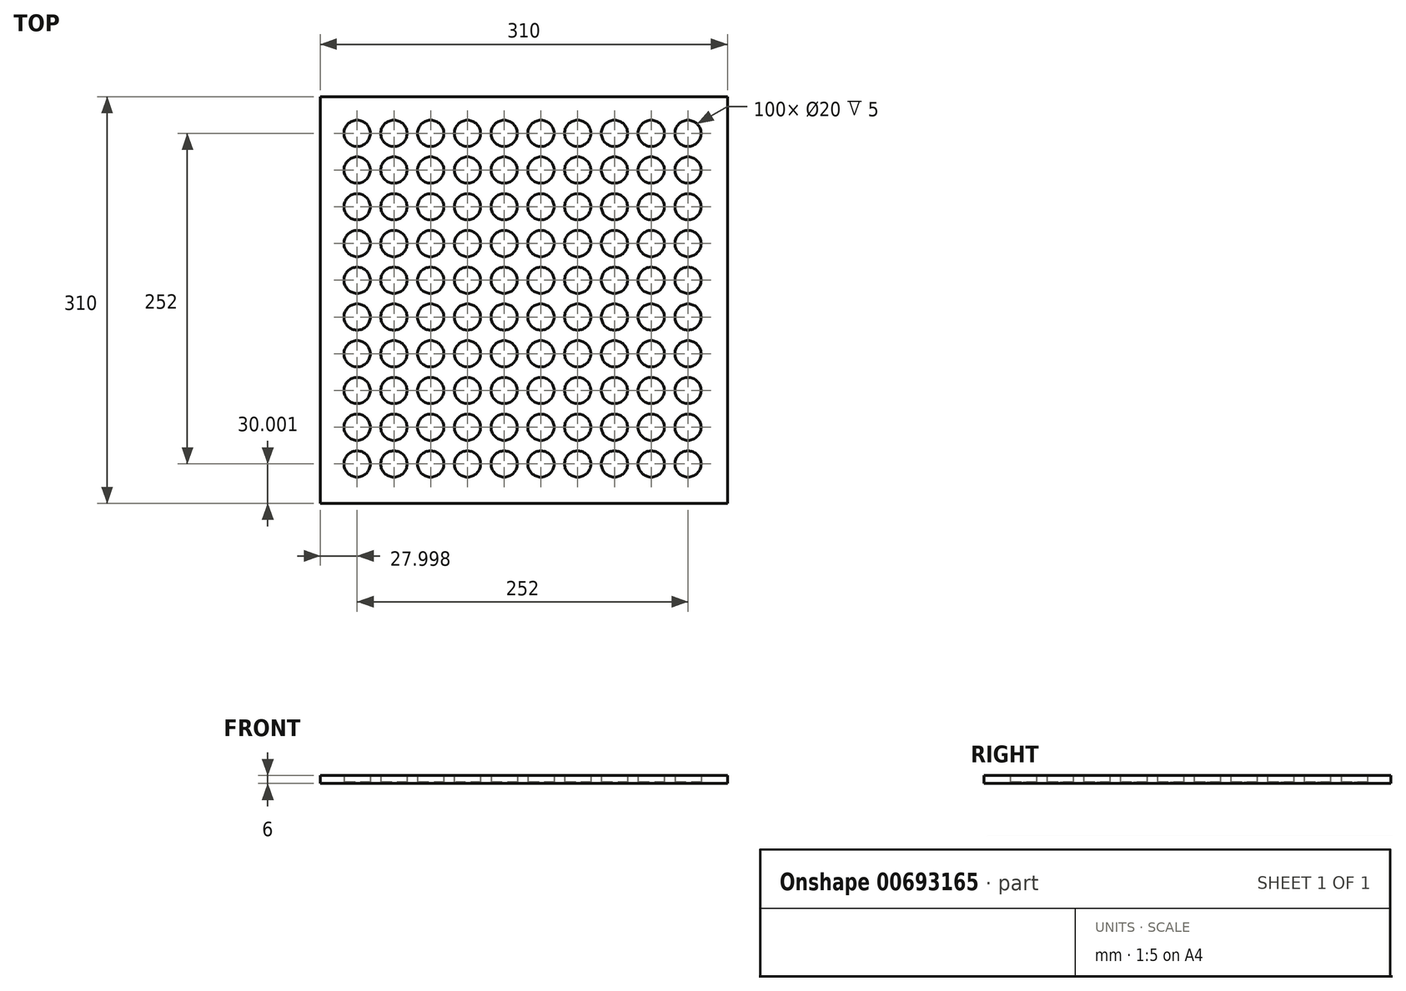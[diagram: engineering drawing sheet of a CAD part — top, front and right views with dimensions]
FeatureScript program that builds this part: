
annotation { "Feature Type Name" : "Feature", "Feature Type Description" : "" }
export const myFeature = defineFeature(function(context is Context, id is Id, definition is map)
    precondition{}
    {
        {
            var Q0;
            Q0=qCreatedBy(makeId("Top.planeOp"),FACE);
            var sketch = newSketch(context, id + "F0", { "sketchPlane" : qUnion([Q0])});
            skLineSegment(sketch, "E0.bottom", {"start": v(-288.8, 191.74) * mm, "end": v(21.2, 191.74) * mm});
            skLineSegment(sketch, "E0.top", {"start": v(-288.8, -118.26) * mm, "end": v(21.2, -118.26) * mm});
            skLineSegment(sketch, "E0.left", {"start": v(-288.8, 191.74) * mm, "end": v(-288.8, -118.26) * mm});
            skLineSegment(sketch, "E0.right", {"start": v(21.2, 191.74) * mm, "end": v(21.2, -118.26) * mm});
            skCircle(sketch, "E1", {"center": v(-260.8, 163.74) * mm, "radius": 10 * mm});
            skCircle(sketch, "E2.0.1.0", {"center": v(-260.8, 135.74) * mm, "radius": 10 * mm});
            skCircle(sketch, "E2.0.2.0", {"center": v(-260.8, 107.74) * mm, "radius": 10 * mm});
            skCircle(sketch, "E2.0.3.0", {"center": v(-260.8, 79.74) * mm, "radius": 10 * mm});
            skCircle(sketch, "E2.0.4.0", {"center": v(-260.8, 51.74) * mm, "radius": 10 * mm});
            skCircle(sketch, "E2.1.0.0", {"center": v(-232.8, 163.74) * mm, "radius": 10 * mm});
            skCircle(sketch, "E2.1.1.0", {"center": v(-232.8, 135.74) * mm, "radius": 10 * mm});
            skCircle(sketch, "E2.1.2.0", {"center": v(-232.8, 107.74) * mm, "radius": 10 * mm});
            skCircle(sketch, "E2.1.3.0", {"center": v(-232.8, 79.74) * mm, "radius": 10 * mm});
            skCircle(sketch, "E2.1.4.0", {"center": v(-232.8, 51.74) * mm, "radius": 10 * mm});
            skCircle(sketch, "E2.2.0.0", {"center": v(-204.8, 163.74) * mm, "radius": 10 * mm});
            skCircle(sketch, "E2.2.1.0", {"center": v(-204.8, 135.74) * mm, "radius": 10 * mm});
            skCircle(sketch, "E2.2.2.0", {"center": v(-204.8, 107.74) * mm, "radius": 10 * mm});
            skCircle(sketch, "E2.2.3.0", {"center": v(-204.8, 79.74) * mm, "radius": 10 * mm});
            skCircle(sketch, "E2.2.4.0", {"center": v(-204.8, 51.74) * mm, "radius": 10 * mm});
            skCircle(sketch, "E2.3.0.0", {"center": v(-176.8, 163.74) * mm, "radius": 10 * mm});
            skCircle(sketch, "E2.3.1.0", {"center": v(-176.8, 135.74) * mm, "radius": 10 * mm});
            skCircle(sketch, "E2.3.2.0", {"center": v(-176.8, 107.74) * mm, "radius": 10 * mm});
            skCircle(sketch, "E2.3.3.0", {"center": v(-176.8, 79.74) * mm, "radius": 10 * mm});
            skCircle(sketch, "E2.3.4.0", {"center": v(-176.8, 51.74) * mm, "radius": 10 * mm});
            skCircle(sketch, "E2.4.0.0", {"center": v(-148.8, 163.74) * mm, "radius": 10 * mm});
            skCircle(sketch, "E2.4.1.0", {"center": v(-148.8, 135.74) * mm, "radius": 10 * mm});
            skCircle(sketch, "E2.4.2.0", {"center": v(-148.8, 107.74) * mm, "radius": 10 * mm});
            skCircle(sketch, "E2.4.3.0", {"center": v(-148.8, 79.74) * mm, "radius": 10 * mm});
            skCircle(sketch, "E2.4.4.0", {"center": v(-148.8, 51.74) * mm, "radius": 10 * mm});
            skCircle(sketch, "E2.5.0.0", {"center": v(-120.8, 163.74) * mm, "radius": 10 * mm});
            skCircle(sketch, "E2.5.1.0", {"center": v(-120.8, 135.74) * mm, "radius": 10 * mm});
            skCircle(sketch, "E2.5.2.0", {"center": v(-120.8, 107.74) * mm, "radius": 10 * mm});
            skCircle(sketch, "E2.5.3.0", {"center": v(-120.8, 79.74) * mm, "radius": 10 * mm});
            skCircle(sketch, "E2.5.4.0", {"center": v(-120.8, 51.74) * mm, "radius": 10 * mm});
            skCircle(sketch, "E2.6.0.0", {"center": v(-92.8, 163.74) * mm, "radius": 10 * mm});
            skCircle(sketch, "E2.6.1.0", {"center": v(-92.8, 135.74) * mm, "radius": 10 * mm});
            skCircle(sketch, "E2.6.2.0", {"center": v(-92.8, 107.74) * mm, "radius": 10 * mm});
            skCircle(sketch, "E2.6.3.0", {"center": v(-92.8, 79.74) * mm, "radius": 10 * mm});
            skCircle(sketch, "E2.6.4.0", {"center": v(-92.8, 51.74) * mm, "radius": 10 * mm});
            skCircle(sketch, "E2.7.0.0", {"center": v(-64.8, 163.74) * mm, "radius": 10 * mm});
            skCircle(sketch, "E2.7.1.0", {"center": v(-64.8, 135.74) * mm, "radius": 10 * mm});
            skCircle(sketch, "E2.7.2.0", {"center": v(-64.8, 107.74) * mm, "radius": 10 * mm});
            skCircle(sketch, "E2.7.3.0", {"center": v(-64.8, 79.74) * mm, "radius": 10 * mm});
            skCircle(sketch, "E2.7.4.0", {"center": v(-64.8, 51.74) * mm, "radius": 10 * mm});
            skCircle(sketch, "E2.8.0.0", {"center": v(-36.8, 163.74) * mm, "radius": 10 * mm});
            skCircle(sketch, "E2.8.1.0", {"center": v(-36.8, 135.74) * mm, "radius": 10 * mm});
            skCircle(sketch, "E2.8.2.0", {"center": v(-36.8, 107.74) * mm, "radius": 10 * mm});
            skCircle(sketch, "E2.8.3.0", {"center": v(-36.8, 79.74) * mm, "radius": 10 * mm});
            skCircle(sketch, "E2.8.4.0", {"center": v(-36.8, 51.74) * mm, "radius": 10 * mm});
            skCircle(sketch, "E2.9.0.0", {"center": v(-8.8, 163.74) * mm, "radius": 10 * mm});
            skCircle(sketch, "E2.9.1.0", {"center": v(-8.8, 135.74) * mm, "radius": 10 * mm});
            skCircle(sketch, "E2.9.2.0", {"center": v(-8.8, 107.74) * mm, "radius": 10 * mm});
            skCircle(sketch, "E2.9.3.0", {"center": v(-8.8, 79.74) * mm, "radius": 10 * mm});
            skCircle(sketch, "E2.9.4.0", {"center": v(-8.8, 51.74) * mm, "radius": 10 * mm});
            skLineSegment(sketch, "E2.direction1", {"start": v(-263.8, 6.74) * mm, "end": v(-235.8, 6.74) * mm, "construction": true});
            skLineSegment(sketch, "E2.direction2", {"start": v(-263.8, 6.74) * mm, "end": v(-263.8, -21.26) * mm, "construction": true});
            skCircle(sketch, "E3.0.0.5", {"center": v(-260.8, 23.74) * mm, "radius": 10 * mm});
            skCircle(sketch, "E3.0.0.6", {"center": v(-260.8, -4.26) * mm, "radius": 10 * mm});
            skCircle(sketch, "E3.0.0.7", {"center": v(-260.8, -32.26) * mm, "radius": 10 * mm});
            skCircle(sketch, "E3.0.0.8", {"center": v(-260.8, -60.26) * mm, "radius": 10 * mm});
            skCircle(sketch, "E3.0.0.9", {"center": v(-260.8, -88.26) * mm, "radius": 10 * mm});
            skCircle(sketch, "E3.0.1.5", {"center": v(-232.8, 23.74) * mm, "radius": 10 * mm});
            skCircle(sketch, "E3.0.1.6", {"center": v(-232.8, -4.26) * mm, "radius": 10 * mm});
            skCircle(sketch, "E3.0.1.7", {"center": v(-232.8, -32.26) * mm, "radius": 10 * mm});
            skCircle(sketch, "E3.0.1.8", {"center": v(-232.8, -60.26) * mm, "radius": 10 * mm});
            skCircle(sketch, "E3.0.1.9", {"center": v(-232.8, -88.26) * mm, "radius": 10 * mm});
            skCircle(sketch, "E3.0.2.5", {"center": v(-204.8, 23.74) * mm, "radius": 10 * mm});
            skCircle(sketch, "E3.0.2.6", {"center": v(-204.8, -4.26) * mm, "radius": 10 * mm});
            skCircle(sketch, "E3.0.2.7", {"center": v(-204.8, -32.26) * mm, "radius": 10 * mm});
            skCircle(sketch, "E3.0.2.8", {"center": v(-204.8, -60.26) * mm, "radius": 10 * mm});
            skCircle(sketch, "E3.0.2.9", {"center": v(-204.8, -88.26) * mm, "radius": 10 * mm});
            skCircle(sketch, "E3.0.3.5", {"center": v(-176.8, 23.74) * mm, "radius": 10 * mm});
            skCircle(sketch, "E3.0.3.6", {"center": v(-176.8, -4.26) * mm, "radius": 10 * mm});
            skCircle(sketch, "E3.0.3.7", {"center": v(-176.8, -32.26) * mm, "radius": 10 * mm});
            skCircle(sketch, "E3.0.3.8", {"center": v(-176.8, -60.26) * mm, "radius": 10 * mm});
            skCircle(sketch, "E3.0.3.9", {"center": v(-176.8, -88.26) * mm, "radius": 10 * mm});
            skCircle(sketch, "E3.0.4.5", {"center": v(-148.8, 23.74) * mm, "radius": 10 * mm});
            skCircle(sketch, "E3.0.4.6", {"center": v(-148.8, -4.26) * mm, "radius": 10 * mm});
            skCircle(sketch, "E3.0.4.7", {"center": v(-148.8, -32.26) * mm, "radius": 10 * mm});
            skCircle(sketch, "E3.0.4.8", {"center": v(-148.8, -60.26) * mm, "radius": 10 * mm});
            skCircle(sketch, "E3.0.4.9", {"center": v(-148.8, -88.26) * mm, "radius": 10 * mm});
            skCircle(sketch, "E3.0.5.5", {"center": v(-120.8, 23.74) * mm, "radius": 10 * mm});
            skCircle(sketch, "E3.0.5.6", {"center": v(-120.8, -4.26) * mm, "radius": 10 * mm});
            skCircle(sketch, "E3.0.5.7", {"center": v(-120.8, -32.26) * mm, "radius": 10 * mm});
            skCircle(sketch, "E3.0.5.8", {"center": v(-120.8, -60.26) * mm, "radius": 10 * mm});
            skCircle(sketch, "E3.0.5.9", {"center": v(-120.8, -88.26) * mm, "radius": 10 * mm});
            skCircle(sketch, "E3.0.6.5", {"center": v(-92.8, 23.74) * mm, "radius": 10 * mm});
            skCircle(sketch, "E3.0.6.6", {"center": v(-92.8, -4.26) * mm, "radius": 10 * mm});
            skCircle(sketch, "E3.0.6.7", {"center": v(-92.8, -32.26) * mm, "radius": 10 * mm});
            skCircle(sketch, "E3.0.6.8", {"center": v(-92.8, -60.26) * mm, "radius": 10 * mm});
            skCircle(sketch, "E3.0.6.9", {"center": v(-92.8, -88.26) * mm, "radius": 10 * mm});
            skCircle(sketch, "E3.0.7.5", {"center": v(-64.8, 23.74) * mm, "radius": 10 * mm});
            skCircle(sketch, "E3.0.7.6", {"center": v(-64.8, -4.26) * mm, "radius": 10 * mm});
            skCircle(sketch, "E3.0.7.7", {"center": v(-64.8, -32.26) * mm, "radius": 10 * mm});
            skCircle(sketch, "E3.0.7.8", {"center": v(-64.8, -60.26) * mm, "radius": 10 * mm});
            skCircle(sketch, "E3.0.7.9", {"center": v(-64.8, -88.26) * mm, "radius": 10 * mm});
            skCircle(sketch, "E3.0.8.5", {"center": v(-36.8, 23.74) * mm, "radius": 10 * mm});
            skCircle(sketch, "E3.0.8.6", {"center": v(-36.8, -4.26) * mm, "radius": 10 * mm});
            skCircle(sketch, "E3.0.8.7", {"center": v(-36.8, -32.26) * mm, "radius": 10 * mm});
            skCircle(sketch, "E3.0.8.8", {"center": v(-36.8, -60.26) * mm, "radius": 10 * mm});
            skCircle(sketch, "E3.0.8.9", {"center": v(-36.8, -88.26) * mm, "radius": 10 * mm});
            skCircle(sketch, "E3.0.9.5", {"center": v(-8.8, 23.74) * mm, "radius": 10 * mm});
            skCircle(sketch, "E3.0.9.6", {"center": v(-8.8, -4.26) * mm, "radius": 10 * mm});
            skCircle(sketch, "E3.0.9.7", {"center": v(-8.8, -32.26) * mm, "radius": 10 * mm});
            skCircle(sketch, "E3.0.9.8", {"center": v(-8.8, -60.26) * mm, "radius": 10 * mm});
            skCircle(sketch, "E3.0.9.9", {"center": v(-8.8, -88.26) * mm, "radius": 10 * mm});
            skSolve(sketch);
        }
        {
            var Q0;
            Q0=qSketchRegion(id+"F0",true);
            extrude(context, id + "F1", {"entities" : qUnion([Q0]), "depth" : 5 * mm, "offsetDistance" : 25 * mm});
        }
        {
            var Q0;
            Q0=makeQuery(id+"F1.opExtrude","CAP_FACE",FACE,{"disambiguationData":[OSD([sQuery(id+"F0.wireOp",EDGE,"E0.bottom"),sQuery(id+"F0.wireOp",EDGE,"E0.top"),sQuery(id+"F0.wireOp",EDGE,"E0.left"),sQuery(id+"F0.wireOp",EDGE,"E0.right"),sQuery(id+"F0.wireOp",EDGE,"Q3saARHD-Gs58-2NVK-PtzY-fhxvJSEAU8xS.bottom"),sQuery(id+"F0.wireOp",EDGE,"Q3saARHD-Gs58-2NVK-PtzY-fhxvJSEAU8xS.top"),sQuery(id+"F0.wireOp",EDGE,"Q3saARHD-Gs58-2NVK-PtzY-fhxvJSEAU8xS.left"),sQuery(id+"F0.wireOp",EDGE,"Q3saARHD-Gs58-2NVK-PtzY-fhxvJSEAU8xS.right"),sQuery(id+"F0.wireOp",EDGE,"dcdc5563-4537-49a2-8787-ece9258b1a45.0.1.0"),sQuery(id+"F0.wireOp",EDGE,"dcdc5563-4537-49a2-8787-ece9258b1a45.0.1.1"),sQuery(id+"F0.wireOp",EDGE,"dcdc5563-4537-49a2-8787-ece9258b1a45.0.1.2"),sQuery(id+"F0.wireOp",EDGE,"dcdc5563-4537-49a2-8787-ece9258b1a45.0.1.3"),sQuery(id+"F0.wireOp",EDGE,"dcdc5563-4537-49a2-8787-ece9258b1a45.0.2.0"),sQuery(id+"F0.wireOp",EDGE,"dcdc5563-4537-49a2-8787-ece9258b1a45.0.2.1"),sQuery(id+"F0.wireOp",EDGE,"dcdc5563-4537-49a2-8787-ece9258b1a45.0.2.2"),sQuery(id+"F0.wireOp",EDGE,"dcdc5563-4537-49a2-8787-ece9258b1a45.0.2.3"),sQuery(id+"F0.wireOp",EDGE,"dcdc5563-4537-49a2-8787-ece9258b1a45.0.3.0"),sQuery(id+"F0.wireOp",EDGE,"dcdc5563-4537-49a2-8787-ece9258b1a45.0.3.1"),sQuery(id+"F0.wireOp",EDGE,"dcdc5563-4537-49a2-8787-ece9258b1a45.0.3.2"),sQuery(id+"F0.wireOp",EDGE,"dcdc5563-4537-49a2-8787-ece9258b1a45.0.3.3"),sQuery(id+"F0.wireOp",EDGE,"dcdc5563-4537-49a2-8787-ece9258b1a45.0.4.0"),sQuery(id+"F0.wireOp",EDGE,"dcdc5563-4537-49a2-8787-ece9258b1a45.0.4.1"),sQuery(id+"F0.wireOp",EDGE,"dcdc5563-4537-49a2-8787-ece9258b1a45.0.4.2"),sQuery(id+"F0.wireOp",EDGE,"dcdc5563-4537-49a2-8787-ece9258b1a45.0.4.3"),sQuery(id+"F0.wireOp",EDGE,"dcdc5563-4537-49a2-8787-ece9258b1a45.0.5.0"),sQuery(id+"F0.wireOp",EDGE,"dcdc5563-4537-49a2-8787-ece9258b1a45.0.5.1"),sQuery(id+"F0.wireOp",EDGE,"dcdc5563-4537-49a2-8787-ece9258b1a45.0.5.2"),sQuery(id+"F0.wireOp",EDGE,"dcdc5563-4537-49a2-8787-ece9258b1a45.0.5.3"),sQuery(id+"F0.wireOp",EDGE,"dcdc5563-4537-49a2-8787-ece9258b1a45.0.6.0"),sQuery(id+"F0.wireOp",EDGE,"dcdc5563-4537-49a2-8787-ece9258b1a45.0.6.1"),sQuery(id+"F0.wireOp",EDGE,"dcdc5563-4537-49a2-8787-ece9258b1a45.0.6.2"),sQuery(id+"F0.wireOp",EDGE,"dcdc5563-4537-49a2-8787-ece9258b1a45.0.6.3")])],"isStart":true});
            var sketch = newSketch(context, id + "F2", { "sketchPlane" : qUnion([Q0])});
            skLineSegment(sketch, "E4.bottom", {"start": v(-288.8, -191.74) * mm, "end": v(21.2, -191.74) * mm});
            skLineSegment(sketch, "E4.top", {"start": v(-288.8, 118.26) * mm, "end": v(21.2, 118.26) * mm});
            skLineSegment(sketch, "E4.left", {"start": v(-288.8, -191.74) * mm, "end": v(-288.8, 118.26) * mm});
            skLineSegment(sketch, "E4.right", {"start": v(21.2, -191.74) * mm, "end": v(21.2, 118.26) * mm});
            skSolve(sketch);
        }
        {
            var Q0;
            Q0=qSketchRegion(id+"F2",true);
            extrude(context, id + "F3", {"entities" : qUnion([Q0]), "operationType" : NewBodyOperationType.ADD, "depth" : 1 * mm, "offsetDistance" : 25 * mm});
        }
    });
